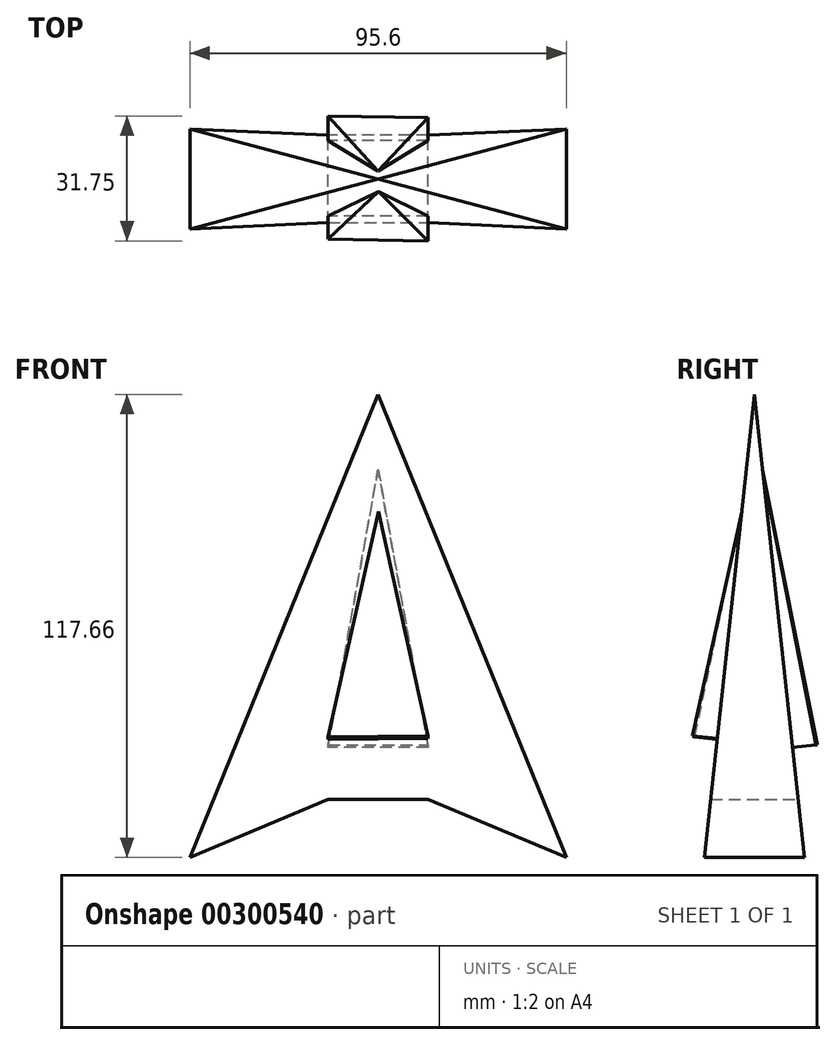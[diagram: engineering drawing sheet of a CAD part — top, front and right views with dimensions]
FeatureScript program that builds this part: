
annotation { "Feature Type Name" : "Feature", "Feature Type Description" : "" }
export const myFeature = defineFeature(function(context is Context, id is Id, definition is map)
    precondition{}
    {
        {
            var Q0;
            Q0=qCreatedBy(makeId("Front.planeOp"),FACE);
            var sketch = newSketch(context, id + "F0", { "sketchPlane" : qUnion([Q0])});
            skLineSegment(sketch, "E0", {"start": v(48.37, -50.4) * mm, "end": v(48.37, -12.3) * mm});
            skLineSegment(sketch, "E1", {"start": v(48.37, -12.3) * mm, "end": v(31.94, 49.04) * mm});
            skPoint(sketch, "E2.endSnap0", {"position": v(19.24, -50.4) * mm});
            skLineSegment(sketch, "E3", {"start": v(19.24, -50.4) * mm, "end": v(19.24, 139.84) * mm, "construction": true});
            skLineSegment(sketch, "E4", {"start": v(31.94, 49.04) * mm, "end": v(19.24, 49.04) * mm});
            skLineSegment(sketch, "E5", {"start": v(48.37, -50.4) * mm, "end": v(19.24, -50.4) * mm});
            skSolve(sketch);
        }
        {
            var Q0;
            Q0 = qSketchRegion(id + "F0", true);
            var Q1;
            Q1=sQuery(id+"F0.wireOp",EDGE,"E1");
            var Q2;
            Q2=sQuery(id+"F0.wireOp",EDGE,"E0");
            var Q3;
            Q3=sQuery(id+"F0.wireOp",EDGE,"E3");
            revolve(context, id + "F1", {"bodyType" : ToolBodyType.SURFACE, "entities" : qUnion([Q0]), "surfaceEntities" : qUnion([Q1, Q2]), "axis" : qUnion([Q3]), "revolveType" : RevolveType.FULL});
        }
        {
            var Q0;
            Q0=qCreatedBy(makeId("Front.planeOp"),FACE);
            var sketch = newSketch(context, id + "F2", { "sketchPlane" : qUnion([Q0])});
            skLineSegment(sketch, "E6.0", {"start": v(6.54, 49.04) * mm, "end": v(31.94, 49.04) * mm});
            skLineSegment(sketch, "E7", {"start": v(-9.9, -12.3) * mm, "end": v(6.54, 49.04) * mm});
            skLineSegment(sketch, "E8", {"start": v(6.54, 49.04) * mm, "end": v(-28.56, 34.22) * mm});
            skLineSegment(sketch, "E9", {"start": v(-28.56, 34.22) * mm, "end": v(19.24, 151.88) * mm});
            skPoint(sketch, "E9.endSnap0", {"position": v(19.24, 49.04) * mm});
            skLineSegment(sketch, "E10", {"start": v(19.24, 151.88) * mm, "end": v(67.04, 34.22) * mm});
            skPoint(sketch, "E10.endSnap0", {"position": v(35.9, 34.22) * mm});
            skLineSegment(sketch, "E11", {"start": v(67.04, 34.22) * mm, "end": v(31.94, 49.04) * mm});
            skSolve(sketch);
        }
        {
            var Q0;
            Q0=makeQuery(id+"F2.imprint","IMPRINT",FACE,{"disambiguationData":[TD([[makeQuery(id+"F2.imprint","IMPRINT",EDGE,{"derivedFrom":sQuery(id+"F2.wireOp",EDGE,"E6.0")}),1.0]])]});
            extrude(context, id + "F3", {"entities" : qUnion([Q0]), "endBound" : BoundingType.SYMMETRIC, "depth" : 25.4 * mm});
        }
        {
            var Q0;
            Q0=qCreatedBy(makeId("Right.planeOp"),FACE);
            var sketch = newSketch(context, id + "F4", { "sketchPlane" : qUnion([Q0])});
            skLineSegment(sketch, "E12.0.0", {"start": v(12.7, 34.22) * mm, "end": v(12.7, 151.88) * mm});
            skLineSegment(sketch, "E12.0.1", {"start": v(12.7, 151.88) * mm, "end": v(-12.7, 151.88) * mm});
            skLineSegment(sketch, "E12.0.2", {"start": v(-12.7, 151.88) * mm, "end": v(-12.7, 34.22) * mm});
            skLineSegment(sketch, "E12.0.3", {"start": v(-12.7, 34.22) * mm, "end": v(12.7, 34.22) * mm});
            skLineSegment(sketch, "E13.0", {"start": v(-12.7, 49.04) * mm, "end": v(12.7, 49.04) * mm});
            skPoint(sketch, "E14.0", {"position": v(12.7, 49.04) * mm});
            skLineSegment(sketch, "E15", {"start": v(-12.7, 34.22) * mm, "end": v(0, 151.88) * mm});
            skLineSegment(sketch, "E16", {"start": v(0, 151.88) * mm, "end": v(12.7, 34.22) * mm});
            skSolve(sketch);
        }
        {
            var Q0;
            {var subQ0=sQuery(id+"F4.wireOp",EDGE,"E12.0.2");var subQ1=sQuery(id+"F4.wireOp",EDGE,"E12.0.1");var subQ2=makeQuery(id+"F4.imprint","INTERSECT",VERTEX,{"derivedFrom":[subQ1,subQ0]});Q0=makeQuery(id+"F4.imprint","IMPRINT",FACE,{"disambiguationData":[TD([[makeQuery(id+"F4.imprint","IMPRINT",EDGE,{"disambiguationData":[TD([[subQ2,-1.0]])],"derivedFrom":subQ0}),1.0]])]});}
            var Q1;
            {var subQ0=sQuery(id+"F4.wireOp",EDGE,"E12.0.1");var subQ1=sQuery(id+"F4.wireOp",EDGE,"E12.0.0");var subQ2=makeQuery(id+"F4.imprint","INTERSECT",VERTEX,{"derivedFrom":[subQ1,subQ0]});Q1=makeQuery(id+"F4.imprint","IMPRINT",FACE,{"disambiguationData":[TD([[makeQuery(id+"F4.imprint","IMPRINT",EDGE,{"disambiguationData":[TD([[subQ2,1.0]])],"derivedFrom":subQ1}),1.0]])]});}
            var Q2;
            {var subQ1=sQuery(id+"F4.wireOp",EDGE,"E12.0.2");var subQ3=sQuery(id+"F4.wireOp",EDGE,"E13.0");var subQ4=makeQuery(id+"F4.imprint","INTERSECT",VERTEX,{"derivedFrom":[subQ1,subQ3]});Q2=makeQuery(id+"F4.imprint","IMPRINT",FACE,{"disambiguationData":[TD([[makeQuery(id+"F4.imprint","IMPRINT",EDGE,{"disambiguationData":[TD([[subQ4,-1.0]])],"derivedFrom":subQ3}),-1.0]])]});}
            var Q3;
            {var subQ1=sQuery(id+"F4.wireOp",EDGE,"E12.0.0");var subQ3=sQuery(id+"F4.wireOp",EDGE,"E13.0");var subQ4=makeQuery(id+"F4.imprint","INTERSECT",VERTEX,{"derivedFrom":[subQ1,subQ3]});Q3=makeQuery(id+"F4.imprint","IMPRINT",FACE,{"disambiguationData":[TD([[makeQuery(id+"F4.imprint","IMPRINT",EDGE,{"disambiguationData":[TD([[subQ4,1.0]])],"derivedFrom":subQ3}),-1.0]])]});}
            extrude(context, id + "F5", {"entities" : qUnion([Q0, Q1, Q2, Q3]), "operationType" : NewBodyOperationType.REMOVE, "endBound" : BoundingType.THROUGH_ALL, "depth" : 12.7 * mm});
        }
        {
            var Q0;
            {var subQ0=sQuery(id+"F4.wireOp",EDGE,"E12.0.2");var subQ1=sQuery(id+"F4.wireOp",EDGE,"E12.0.1");var subQ2=makeQuery(id+"F4.imprint","INTERSECT",VERTEX,{"derivedFrom":[subQ1,subQ0]});Q0=makeQuery(id+"F4.imprint","IMPRINT",FACE,{"disambiguationData":[TD([[makeQuery(id+"F4.imprint","IMPRINT",EDGE,{"disambiguationData":[TD([[subQ2,-1.0]])],"derivedFrom":subQ0}),1.0]])]});}
            var Q1;
            {var subQ0=sQuery(id+"F4.wireOp",EDGE,"E12.0.1");var subQ1=sQuery(id+"F4.wireOp",EDGE,"E12.0.0");var subQ2=makeQuery(id+"F4.imprint","INTERSECT",VERTEX,{"derivedFrom":[subQ1,subQ0]});Q1=makeQuery(id+"F4.imprint","IMPRINT",FACE,{"disambiguationData":[TD([[makeQuery(id+"F4.imprint","IMPRINT",EDGE,{"disambiguationData":[TD([[subQ2,1.0]])],"derivedFrom":subQ1}),1.0]])]});}
            var Q2;
            {var subQ1=sQuery(id+"F4.wireOp",EDGE,"E12.0.0");var subQ3=sQuery(id+"F4.wireOp",EDGE,"E13.0");var subQ4=makeQuery(id+"F4.imprint","INTERSECT",VERTEX,{"derivedFrom":[subQ1,subQ3]});Q2=makeQuery(id+"F4.imprint","IMPRINT",FACE,{"disambiguationData":[TD([[makeQuery(id+"F4.imprint","IMPRINT",EDGE,{"disambiguationData":[TD([[subQ4,1.0]])],"derivedFrom":subQ3}),-1.0]])]});}
            var Q3;
            {var subQ1=sQuery(id+"F4.wireOp",EDGE,"E12.0.2");var subQ3=sQuery(id+"F4.wireOp",EDGE,"E13.0");var subQ4=makeQuery(id+"F4.imprint","INTERSECT",VERTEX,{"derivedFrom":[subQ1,subQ3]});Q3=makeQuery(id+"F4.imprint","IMPRINT",FACE,{"disambiguationData":[TD([[makeQuery(id+"F4.imprint","IMPRINT",EDGE,{"disambiguationData":[TD([[subQ4,-1.0]])],"derivedFrom":subQ3}),-1.0]])]});}
            extrude(context, id + "F6", {"entities" : qUnion([Q0, Q1, Q2, Q3]), "operationType" : NewBodyOperationType.REMOVE, "endBound" : BoundingType.THROUGH_ALL, "oppositeDirection" : true, "depth" : 25.4 * mm});
        }
        {
            var Q0;
            {var subQ0=sQuery(id+"F4.wireOp",EDGE,"E16");Q0=makeQuery(id+"F6.boolean.opBoolean","MERGE",FACE,{"derivedFrom":[makeQuery(id+"F5.boolean.opBoolean","COPY",FACE,{"derivedFrom":makeQuery(id+"F5.opExtrude","SWEPT_FACE",FACE,{"disambiguationData":[OSD([subQ0])]})}),makeQuery(id+"F6.opExtrude","SWEPT_FACE",FACE,{"disambiguationData":[OSD([subQ0])]})]});}
            var sketch = newSketch(context, id + "F7", { "sketchPlane" : qUnion([Q0])});
            skLineSegment(sketch, "E17", {"start": v(-19.24, 131.8) * mm, "end": v(-31.94, 60.76) * mm});
            skLineSegment(sketch, "E18", {"start": v(-31.94, 60.76) * mm, "end": v(-6.54, 60.76) * mm});
            skLineSegment(sketch, "E19", {"start": v(-6.54, 60.76) * mm, "end": v(-19.24, 131.8) * mm});
            skSolve(sketch);
        }
        {
            var Q0;
            Q0=makeQuery(id+"F7.imprint","IMPRINT",FACE,{"disambiguationData":[TD([[makeQuery(id+"F7.imprint","IMPRINT",EDGE,{"derivedFrom":sQuery(id+"F7.wireOp",EDGE,"E17")}),1.0]])]});
            extrude(context, id + "F8", {"entities" : qUnion([Q0]), "operationType" : NewBodyOperationType.ADD, "depth" : 6.35 * mm});
        }
        {
            var Q0;
            Q0=makeQuery(id+"F8.opExtrude","SWEPT_FACE",FACE,{"disambiguationData":[OSD([sQuery(id+"F7.wireOp",EDGE,"E19")])]});
            var sketch = newSketch(context, id + "F9", { "sketchPlane" : qUnion([Q0])});
            skLineSegment(sketch, "E20.0", {"start": v(-9.77, 62.34) * mm, "end": v(-2.14, 134.1) * mm});
            skPoint(sketch, "E21.0", {"position": v(-12.92, 62.68) * mm});
            skLineSegment(sketch, "E22.0", {"start": v(-9.3, 66.79) * mm, "end": v(-9.77, 62.34) * mm});
            skLineSegment(sketch, "E23.0", {"start": v(-16.08, 63.01) * mm, "end": v(-8.46, 134.78) * mm});
            skLineSegment(sketch, "E24.0", {"start": v(-15.6, 67.46) * mm, "end": v(-16.08, 63.01) * mm});
            skLineSegment(sketch, "E25", {"start": v(-16.08, 63.01) * mm, "end": v(-2.14, 134.1) * mm});
            skSolve(sketch);
        }
        {
            var Q0;
            Q0=makeQuery(id+"F9.imprint","IMPRINT",FACE,{"disambiguationData":[TD([[makeQuery(id+"F9.imprint","IMPRINT",EDGE,{"derivedFrom":sQuery(id+"F9.wireOp",EDGE,"E23.0")}),-1.0]])]});
            extrude(context, id + "F10", {"entities" : qUnion([Q0]), "operationType" : NewBodyOperationType.REMOVE, "endBound" : BoundingType.THROUGH_ALL, "oppositeDirection" : true, "depth" : 25.4 * mm});
        }
        {
            var Q0;
            {var subQ0=sQuery(id+"F4.wireOp",EDGE,"E15");Q0=makeQuery(id+"F6.boolean.opBoolean","MERGE",FACE,{"derivedFrom":[makeQuery(id+"F5.boolean.opBoolean","COPY",FACE,{"derivedFrom":makeQuery(id+"F5.opExtrude","SWEPT_FACE",FACE,{"disambiguationData":[OSD([subQ0])]})}),makeQuery(id+"F6.opExtrude","SWEPT_FACE",FACE,{"disambiguationData":[OSD([subQ0])]})]});}
            var sketch = newSketch(context, id + "F11", { "sketchPlane" : qUnion([Q0])});
            skPoint(sketch, "E26.0", {"position": v(19.3, 121.08) * mm});
            skPoint(sketch, "E27.0", {"position": v(6.54, 62.84) * mm});
            skPoint(sketch, "E28.0", {"position": v(31.93, 63.09) * mm});
            skLineSegment(sketch, "E29", {"start": v(6.54, 62.84) * mm, "end": v(19.3, 121.08) * mm});
            skLineSegment(sketch, "E30", {"start": v(19.3, 121.08) * mm, "end": v(31.93, 63.09) * mm});
            skLineSegment(sketch, "E31", {"start": v(31.93, 63.09) * mm, "end": v(6.54, 62.84) * mm});
            skSolve(sketch);
        }
        {
            var Q0;
            Q0=makeQuery(id+"F11.imprint","IMPRINT",FACE,{"disambiguationData":[TD([[makeQuery(id+"F11.imprint","IMPRINT",EDGE,{"derivedFrom":sQuery(id+"F11.wireOp",EDGE,"E29")}),-1.0]])]});
            extrude(context, id + "F12", {"entities" : qUnion([Q0]), "operationType" : NewBodyOperationType.ADD, "depth" : 6.35 * mm});
        }
        {
            var Q0;
            Q0=makeQuery(id+"F12.opExtrude","SWEPT_FACE",FACE,{"disambiguationData":[OSD([sQuery(id+"F11.wireOp",EDGE,"E30")])]});
            var sketch = newSketch(context, id + "F13", { "sketchPlane" : qUnion([Q0])});
            skPoint(sketch, "E32.0", {"position": v(-13.61, 56.59) * mm});
            skLineSegment(sketch, "E33.0", {"start": v(-16.77, 56.92) * mm, "end": v(-10.46, 56.25) * mm});
            skLineSegment(sketch, "E34.0", {"start": v(-10.55, 115.94) * mm, "end": v(-16.77, 56.92) * mm});
            skLineSegment(sketch, "E35.0", {"start": v(-16.77, 56.92) * mm, "end": v(-16.23, 62.05) * mm});
            skLineSegment(sketch, "E36.0", {"start": v(-4.23, 115.28) * mm, "end": v(-10.46, 56.25) * mm});
            skLineSegment(sketch, "E37.0", {"start": v(-10.55, 115.94) * mm, "end": v(-4.23, 115.28) * mm});
            skLineSegment(sketch, "E38", {"start": v(-16.77, 56.92) * mm, "end": v(-4.23, 115.28) * mm});
            skSolve(sketch);
        }
        {
            var Q0;
            Q0=makeQuery(id+"F13.imprint","IMPRINT",FACE,{"disambiguationData":[TD([[makeQuery(id+"F13.imprint","IMPRINT",EDGE,{"derivedFrom":sQuery(id+"F13.wireOp",EDGE,"E34.0")}),1.0]])]});
            extrude(context, id + "F14", {"entities" : qUnion([Q0]), "operationType" : NewBodyOperationType.REMOVE, "endBound" : BoundingType.THROUGH_ALL, "oppositeDirection" : true, "depth" : 25.4 * mm});
        }
    });
